# Revit family: FP_Revit_18_HP90IHCB3_Rangehood_90000963A
name_source: partatom
category: Specialty Equipment
revit_build: Autodesk Revit 2018 (Build: 20170223_1515(x64)
units: mm (PartAtom-declared; Revit-internal decimal feet)

## family parameters
Always vertical = Yes
Cut with Voids When Loaded = Yes
OmniClass Number = 23.40.40.00
OmniClass Title = Food Service Equipment and Furnishings
Part Type = Normal
Room Calculation Point = No
Round Connector Dimension = Use Diameter
Shared = No
Work Plane-Based = No

## types (1)
- FP_Revit_18_HP90IHCB3_Rangehood_90000963A
    Cavity - Depth = 260 mm  [stored 0.853018 ft]
    Cavity - Height = 365 mm  [stored 1.19751 ft]
    Cavity - Width = 800 mm  [stored 2.62467 ft]
    Chassis - Depth = 255 mm  [stored 0.836614 ft]
    Chassis - Height = 315 mm  [stored 1.03346 ft]
    Chassis - Width = 492 mm  [stored 1.61417 ft]
    Connector Description - Electrical = 220-240 V, 50Hz, 15 A fused electrical supply
    Connector Description - Extraction = Use rigid or semi-rigid ducting 150mm diameter, 687m³/hr
    Description = 90cm Built-in Integrated Rangehood
    Manufacturer = Fisher & Paykel Appliances
    Material - Body = Fisher & Paykel - Grey
    Material - Diffuser = Fisher & Paykel - White Bezel
    Material - Glass = Fisher & Paykel - Glass, Black
    Material - Trim = Fisher & Paykel - Stainless Steel
    Model = HP90IHCB3
    Product - Depth = 280 mm  [stored 0.918635 ft]
    Product - Height = 360 mm  [stored 1.1811 ft]
    Product - Width = 530 mm  [stored 1.73885 ft]
    URL = www.fisherpaykel.com
    Visibility - Clearance Required = Yes

note: [stored X ft] marks values corroborated as IEEE doubles in the binary element streams (Revit-internal decimal feet)

## geometry (parser evidence)
native form markers: Sweep x2
no freeform markers — native parametric forms only
